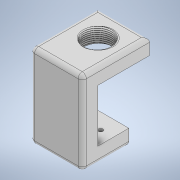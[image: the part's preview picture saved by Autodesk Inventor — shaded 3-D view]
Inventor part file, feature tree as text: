
AUTODESK INVENTOR PART (.ipt)
format: ipt  version: 2021 (Build 250183000, 183)  size: 499,200 bytes
history: native  units: in
note: dims shown in document units (in); Inventor stores cm internally (conversion verified against a paired STEP export)
features: sketch x8, extrude x7, projected_geometry x4, fillet x2, chamfer x1, plane x1, other x1, helix x1
ambient origin geometry x8: Origin, YZ Plane, XZ Plane, XY Plane, X Axis, Y Axis, Z Axis, Center Point
bodies: Solid1 (feature_tree)
feature tree (25):
  extrude  "Extrusion1"  Depth=0.5906in
  extrude  "Extrusion2"  Depth=1.9685in
  extrude  "Extrusion3"  Depth=0.5906in TaperAngle=0.0deg
  chamfer  "Chamfer1"  Distance=1.1811in
  fillet  "Fillet1"  Radius=0.1575in
  extrude  "Extrusion4"  Depth=0.5906in TaperAngle=0.0deg
  extrude  "Extrusion5"  Depth=0.5906in
  extrude  "Extrusion6"  Depth=0.0669in TaperAngle=0.0deg
  sketch  "Sketch7"  dims[d13=0.0787in d14=0.0787in d15=45.0deg d16=0.1575in]
  fillet  "Fillet2"  Radius=0.1575in
  extrude  "Extrusion7"  Depth=0.0669in
  plane  "Work Plane2"
  sketch  "Sketch8"  dims[d17=0.9094in d18=0.0in d19=0.5906in d20=0.0in d21=0.5906in d22=1.9685in d23=0.0in d31=0.1575in d32=0.9843in d33=0.9843in d34=1.063in d35=1.9685in d36=0.0in d37=-0.9843in d38=0.0787in d39=0.0295in d40=0.0787in d41=0.0079in d42=0.0669in d43=2.2343in d44=0.3937in d45=0.0in d46=90.0deg d47=90.0deg d48=0.0in d49=0.0in]
  other  "Work Axis1"
  helix  "Coil1"  [1 undecoded]
  sketch  "Sketch1"  dims[d0=1.6811in d1=0.5906in]
  sketch  "Sketch2"  dims[d2=3.1496in d3=1.9685in]
  sketch  "Sketch3"  dims[d4=0.5906in d5=0.0in d6=1.1811in d7=0.0in]
  sketch  "Sketch4"  dims[d8=0.1575in]
  sketch  "Sketch5"  dims[d9=0.4724in]
  sketch  "Sketch6"  dims[d10=0.4724in d11=1.1811in d12=0.0in]
  projected_geometry  "Projected Loop1"
  projected_geometry  "Project Cut Edges1"
  projected_geometry  "Project Cut Edges2"
  projected_geometry  "Project Cut Edges3"
note: 1 required parameter value undecoded (feature->parameter linkage not recoverable at this tier; creation-order binding heuristic only, values carry confidence <= 0.55)
